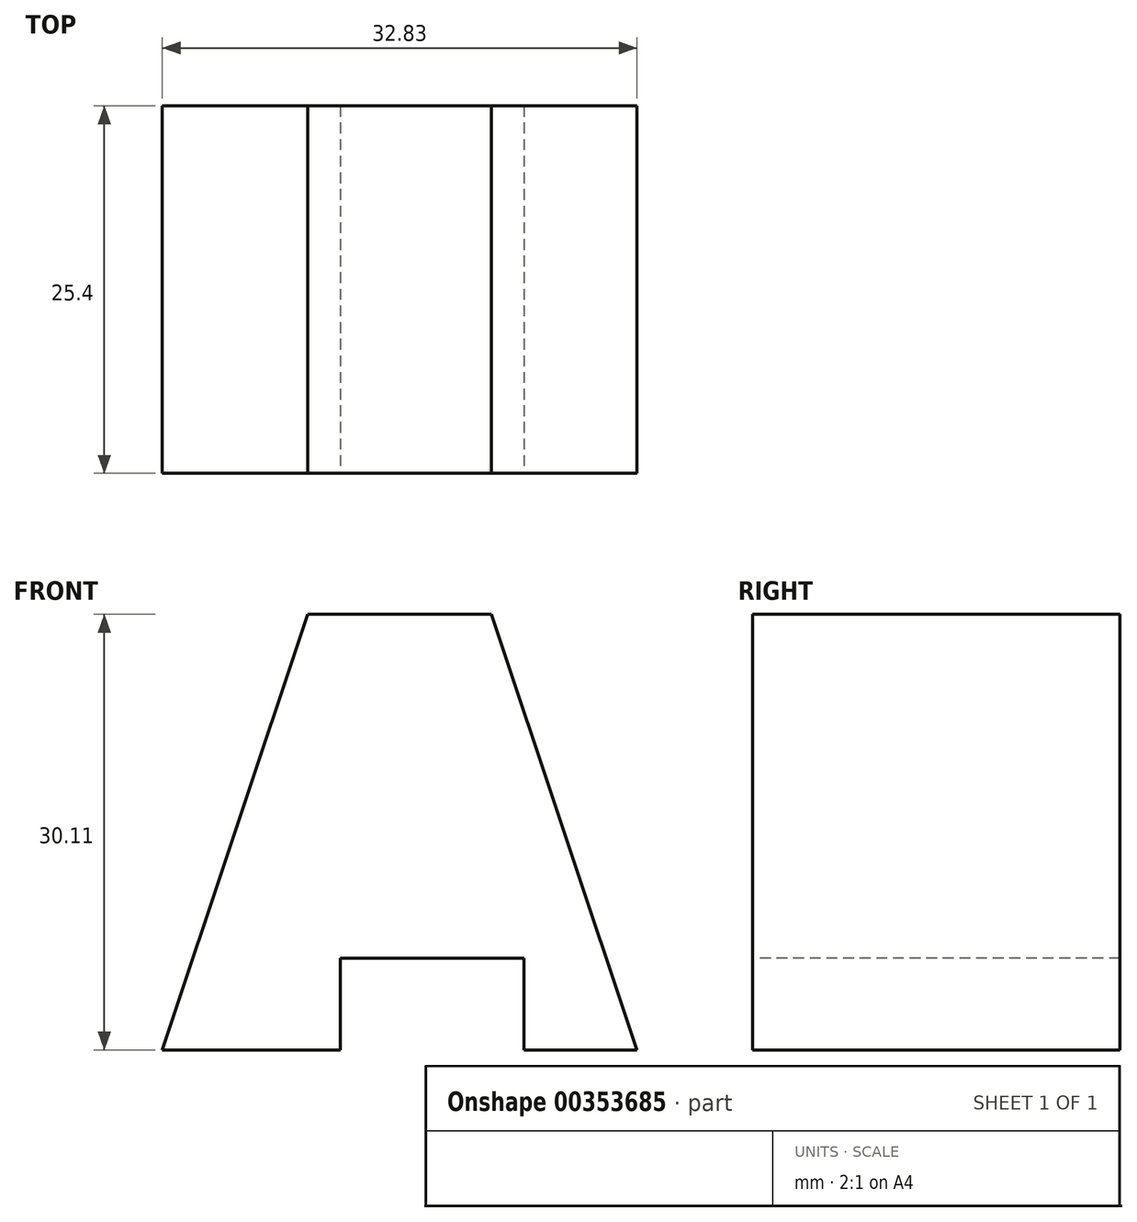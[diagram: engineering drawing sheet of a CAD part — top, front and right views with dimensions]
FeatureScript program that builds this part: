
annotation { "Feature Type Name" : "Feature", "Feature Type Description" : "" }
export const myFeature = defineFeature(function(context is Context, id is Id, definition is map)
    precondition{}
    {
        {
            var Q0;
            Q0=qCreatedBy(makeId("Front.planeOp"),FACE);
            var sketch = newSketch(context, id + "F0", { "sketchPlane" : qUnion([Q0])});
            skLineSegment(sketch, "E0", {"start": v(1.75, 30.11) * mm, "end": v(14.45, 30.11) * mm});
            skLineSegment(sketch, "E1", {"start": v(1.75, 30.11) * mm, "end": v(-8.32, 0) * mm});
            skLineSegment(sketch, "E2", {"start": v(-13.59, 0) * mm, "end": v(24.51, 0) * mm});
            skLineSegment(sketch, "E3", {"start": v(14.45, 30.11) * mm, "end": v(24.51, 0) * mm});
            skSolve(sketch);
        }
        {
            var Q0;
            Q0=makeQuery(id+"F0.imprint","IMPRINT",FACE,{"disambiguationData":[TD([[makeQuery(id+"F0.imprint","IMPRINT",EDGE,{"derivedFrom":sQuery(id+"F0.wireOp",EDGE,"E0")}),-1.0]])]});
            extrude(context, id + "F1", {"entities" : qUnion([Q0]), "depth" : 25.4 * mm});
        }
        {
            var Q0;
            Q0=makeQuery(id+"F1.opExtrude","CAP_FACE",FACE,{"disambiguationData":[OSD([sQuery(id+"F0.wireOp",EDGE,"E0"),sQuery(id+"F0.wireOp",EDGE,"E1"),sQuery(id+"F0.wireOp",EDGE,"E2"),sQuery(id+"F0.wireOp",EDGE,"E3")])],"isStart":false});
            var sketch = newSketch(context, id + "F2", { "sketchPlane" : qUnion([Q0])});
            skLineSegment(sketch, "E4", {"start": v(4, 0) * mm, "end": v(4, 6.35) * mm});
            skLineSegment(sketch, "E5", {"start": v(4, 6.35) * mm, "end": v(16.7, 6.35) * mm});
            skLineSegment(sketch, "E6", {"start": v(16.7, 6.35) * mm, "end": v(16.7, 0) * mm});
            skSolve(sketch);
        }
        {
            var Q0;
            {var subQ0=sQuery(id+"F2.wireOp",EDGE,"E4");Q0=makeQuery(id+"F2.imprint","IMPRINT",FACE,{"disambiguationData":[TD([[makeQuery(id+"F2.imprint","IMPRINT",EDGE,{"derivedFrom":subQ0}),-1.0]])]});}
            extrude(context, id + "F3", {"entities" : qUnion([Q0]), "operationType" : NewBodyOperationType.REMOVE, "oppositeDirection" : true, "depth" : 25.4 * mm});
        }
    });
